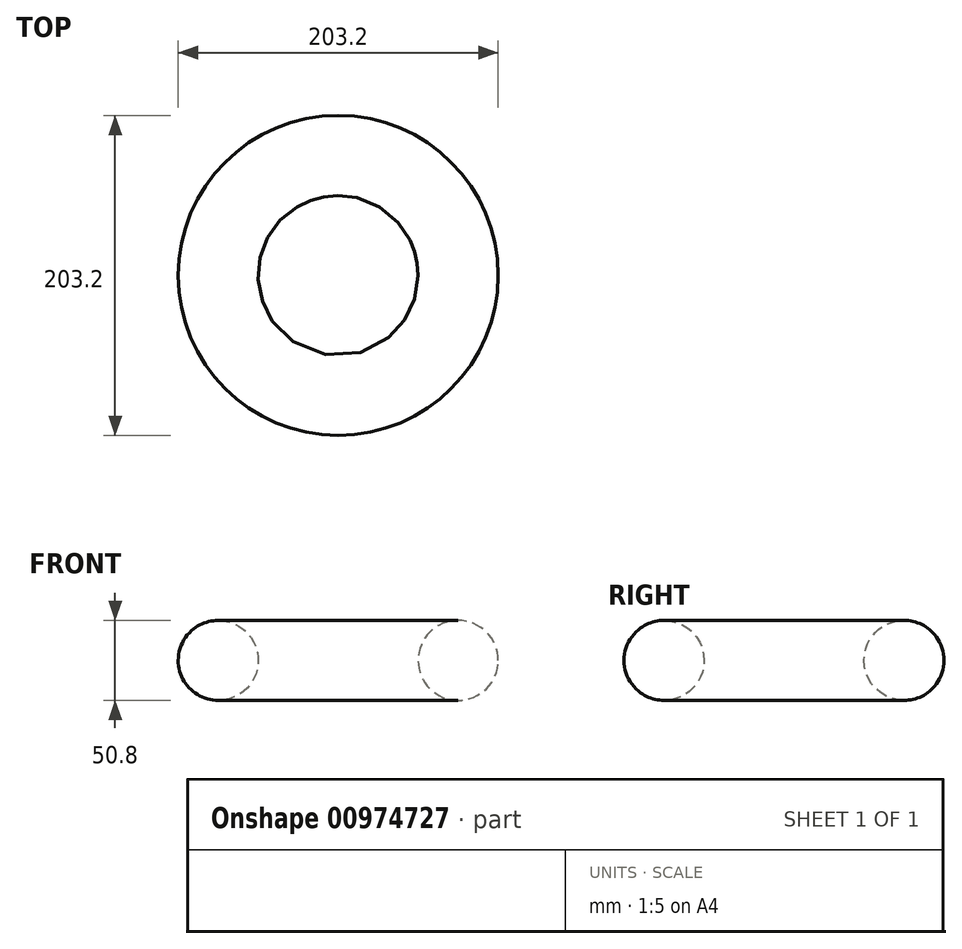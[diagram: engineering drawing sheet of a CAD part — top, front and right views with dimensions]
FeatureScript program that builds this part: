
annotation { "Feature Type Name" : "Feature", "Feature Type Description" : "" }
export const myFeature = defineFeature(function(context is Context, id is Id, definition is map)
    precondition{}
    {
        {
            var Q0;
            Q0=qCreatedBy(makeId("Front.planeOp"),FACE);
            var sketch = newSketch(context, id + "F0", { "sketchPlane" : qUnion([Q0])});
            skCircle(sketch, "E0", {"center": v(0, 0) * mm, "radius": 25.4 * mm});
            skSolve(sketch);
        }
        {
            var Q0;
            Q0=qCreatedBy(makeId("Top.planeOp"),FACE);
            var sketch = newSketch(context, id + "F1", { "sketchPlane" : qUnion([Q0])});
            skCircle(sketch, "E1", {"center": v(-76.2, 0) * mm, "radius": 76.2 * mm});
            skSolve(sketch);
        }
        {
            var Q0;
            Q0=makeQuery(id+"F0.imprint","IMPRINT",FACE,{"disambiguationData":[TD([[makeQuery(id+"F0.imprint","IMPRINT",EDGE,{"derivedFrom":sQuery(id+"F0.wireOp",EDGE,"E0")}),1.0]])]});
            var Q1;
            Q1=sQuery(id+"F1.wireOp",EDGE,"E1");
            sweep(context, id + "F2", {"profiles" : qUnion([Q0]), "path" : qUnion([Q1])});
        }
    });
